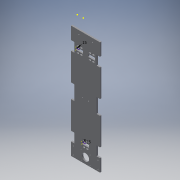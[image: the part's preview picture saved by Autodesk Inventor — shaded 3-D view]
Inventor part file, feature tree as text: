
AUTODESK INVENTOR PART (.ipt)
format: ipt  version: 2019 (Build 230136000, 136)  size: 266,240 bytes
history: native  units: in
note: dims shown in document units (in); Inventor stores cm internally (conversion verified against a paired STEP export)
features: reference x6, other x4, sketch x3, extrude x1
ambient origin geometry x8: Origin, YZ Plane, XZ Plane, XY Plane, X Axis, Y Axis, Z Axis, Center Point
bodies: Solid1 (feature_tree)
feature tree (14):
  extrude  "Extrusion1"  Depth=0.3465in
  sketch  "Sketch2"  dims[d3=3.937in]
  sketch  "Sketch3"  dims[d4=0.1969in d5=0.0in d6=0.5906in d8=0.5906in d9=2.1654in d10=2.1654in d11=0.128in d12=1.2205in d13=0.1969in d14=0.9843in d15=0.1575in d16=0.315in d17=0.1575in d18=0.0984in d19=0.1673in d20=0.1673in d21=1.8504in d22=0.4724in d23=0.1673in d24=0.1673in d25=1.063in d26=0.2756in d27=0.1673in d28=0.1673in d29=1.2598in d30=0.4724in d31=1.9685in d32=0.1673in d33=0.1673in d34=0.7874in d35=0.9843in]
  sketch  "Sketch1"  dims[d1=0.9449in d2=0.3465in]
  reference  "Reference1"
  reference  "Reference2"
  reference  "Reference3"
  reference  "Reference4"
  reference  "Reference5"
  reference  "Reference6"
  other  "<userpath>\Stuff\Ajedrez2\XCart.iam"
  other  "XCart.iam"
  other  "YPulleySupport:1"
  other  "YPulleySupportBase:1"
